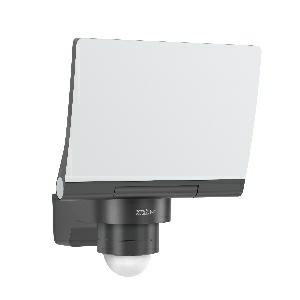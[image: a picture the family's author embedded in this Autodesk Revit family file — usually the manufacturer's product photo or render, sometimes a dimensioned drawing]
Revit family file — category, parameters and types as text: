
# Revit family: xled_pro_240_068066
name_source: partatom
category: Leuchten
revit_build: Autodesk Revit 2016 (Build: 20190508_0715(x64)
units: mm (PartAtom-declared; Revit-internal decimal feet)

## family parameters
Basisbauteil = Fläche
Beim Laden mit Abzugskörper schneiden = Nein
Bemaßung runder Anschluss = Durchmesser verwenden
Gemeinsam genutzt = Nein
Lichtquelle = Nein
Raumberechnungspunkt = Nein
Teiletyp = Normal

## types (1)
- XLED PRO 240 (1 x , 2120 lm, 3000 K)
    Beschreibung = Dimensions (L x W x H): 161 x 180 x 221 mm; Mains power supply: 230 – 240 V / 50 – 60 Hz; Mounting height max.: 6,00 m; Sensor Technology: passive infrared; Output: 20 W; Interconnection: Yes; Switching output 1, resistive: 1000 W; Luminous flux: 2120 lm; Colour temperature: 3000 K; Colour variation LED: SDCM3; Colour Rendering Index CRI: 80-89; With lamp: Yes, STEINEL LED system; Lamp: LED cannot be replaced; LED life expectancy (max. °C): 60000 h; Drop in luminous flux in accordance with LM80: L70B10; LED cooling system: HCMC (High Conductive Magnesium Composite); With motion detector: Yes; Detection angle: 240 °; Angle of aperture: 180 °; Sneak-by guard: Yes; Capability of masking out individual segments: Yes; Reach, radial: r = 3 m (19 m²); Reach, tangential: r = 12 m (302 m²); Photo-cell controller: Yes; Twilight setting: 2 – 1000 lx; Time setting: 10 sec – 15 min; Basic light level function: No; Soft light start: No; Continuous light: selectable; Impact resistance: IK03; IP-rating: IP44; Protection class: II; Ambient temperature: -20 – 40 °C; Housing material: HCMC; Cover material: Plastic, opal; Manufacturer's Warranty: 5 years; Includes corner wall mount: Yes; PU1, net weight: 0,64 kg; Version: warm white anthracite; PU1, EAN: 4007841068066
    Color Rendering = 80-89
    Color Temperature = 3000 K
    Frequency = 60 Hz, 50 Hz
    Height = 221 mm
    Hersteller = Steinel
    Lamp Light Flux = 2120 lm
    Lamp count = 1
    Lampe = 1 x
    Length = 161 mm
    Luminous efficacy = 0 lm/W
    ModVariant = Nein
    Modell = 068066
    Mounting Type = Surface mounted
    Number of Poles = 1
    OnlyDefault = Ja
    Power Factor = 1
    Product Name = XLED PRO 240
    Product group = Sensor-switched indoor light
    ProductGroupID = 30
    Protection Class = Protection class II
    Protection Degree = IP 34
    RlxData = <blob elided: 71745 chars, md5=de1c63ed>
    Scheinlast = 20 VA
    Socket = socket
    Standby Power = 0 W
    System Light Flux = 0 lm
    System Power = 20 W
    Typenbild = produkt1_068066.jpg
    Typenkommentare = Product without accessories
    URL = http://relux.com
    VarID = ---
    Voltage = 0 V
    Vorgabe-Ansicht = 1800 mm
    Weight = 0.00 kg
    Width = 180 mm  [stored 0.590551 ft]

note: [stored X ft] marks values corroborated as IEEE doubles in the binary element streams (Revit-internal decimal feet)

## geometry (parser evidence)
native form markers: Sweep x16
no freeform markers — native parametric forms only
